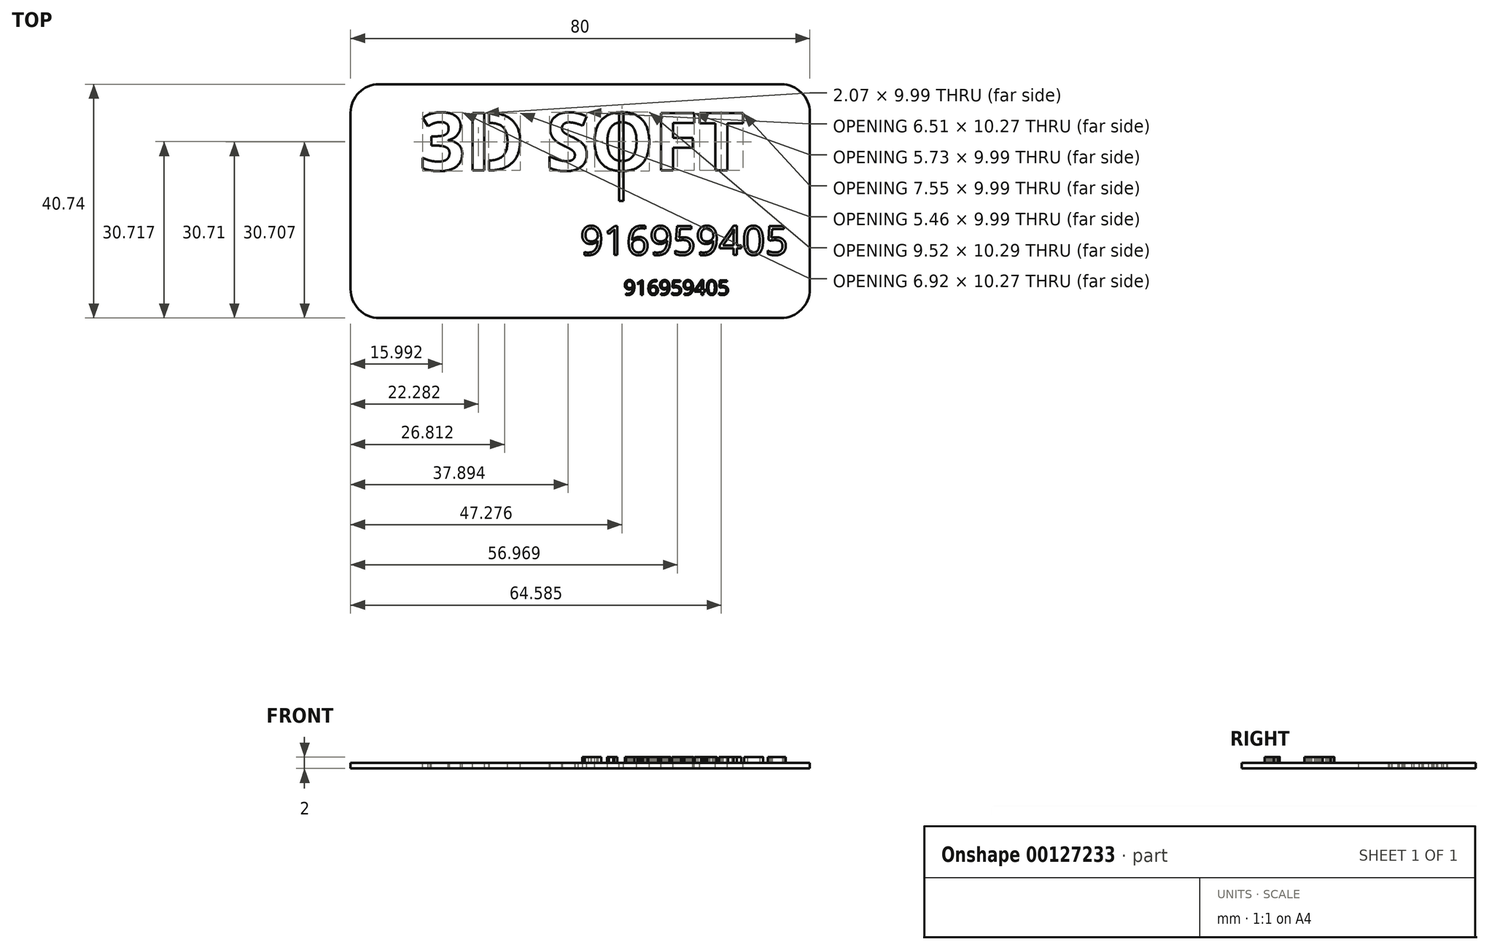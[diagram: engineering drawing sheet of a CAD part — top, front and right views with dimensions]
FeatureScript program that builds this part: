
annotation { "Feature Type Name" : "Feature", "Feature Type Description" : "" }
export const myFeature = defineFeature(function(context is Context, id is Id, definition is map)
    precondition{}
    {
        {
            var Q0;
            Q0=qCreatedBy(makeId("Top.planeOp"),FACE);
            var sketch = newSketch(context, id + "F0", { "sketchPlane" : qUnion([Q0])});
            skLineSegment(sketch, "E0.bottom", {"start": v(40, 20.37) * mm, "end": v(-40, 20.37) * mm});
            skLineSegment(sketch, "E0.top", {"start": v(40, -20.37) * mm, "end": v(-40, -20.37) * mm});
            skLineSegment(sketch, "E0.left", {"start": v(40, 20.37) * mm, "end": v(40, -20.37) * mm});
            skLineSegment(sketch, "E0.right", {"start": v(-40, 20.37) * mm, "end": v(-40, -20.37) * mm});
            skPoint(sketch, "E0.middle", {"position": v(0, 0) * mm});
            skSolve(sketch);
        }
        {
            var Q0;
            Q0=makeQuery(id+"F0.imprint","IMPRINT",FACE,{"disambiguationData":[TD([[makeQuery(id+"F0.imprint","IMPRINT",EDGE,{"derivedFrom":sQuery(id+"F0.wireOp",EDGE,"E0.bottom")}),1.0]])]});
            extrude(context, id + "F1", {"entities" : qUnion([Q0]), "depth" : 1 * mm});
        }
        {
            var Q0;
            Q0=makeQuery(id+"F1.opExtrude","CAP_FACE",FACE,{"disambiguationData":[OSD([sQuery(id+"F0.wireOp",EDGE,"E0.bottom"),sQuery(id+"F0.wireOp",EDGE,"E0.top"),sQuery(id+"F0.wireOp",EDGE,"E0.left"),sQuery(id+"F0.wireOp",EDGE,"E0.right")])],"isStart":false});
            var sketch = newSketch(context, id + "F2", { "sketchPlane" : qUnion([Q0])});
            skText(sketch, "E1", { "text": "3D SOFT", "fontName": "OpenSans-Bold.ttf"});
            const initialGuessF2  = {"E1": [-0.028, 0.00534, 1, 0, 0.01008]};
            skSetInitialGuess(sketch, initialGuessF2);
            skSolve(sketch);
        }
        {
            var Q0;
            Q0 = qSketchRegion(id + "F2", true);
            extrude(context, id + "F3", {"entities" : qUnion([Q0]), "operationType" : NewBodyOperationType.REMOVE, "oppositeDirection" : true, "depth" : 25 * mm});
        }
        {
            var Q0;
            {var subQ0=sQuery(id+"F0.wireOp",EDGE,"E0.top");var subQ1=sQuery(id+"F0.wireOp",EDGE,"E0.right");var subQ2=sQuery(id+"F0.wireOp",EDGE,"E0.bottom");var subQ3=sQuery(id+"F0.wireOp",EDGE,"E0.left");Q0=makeQuery(id+"F3.boolean.opBoolean","SPLIT",FACE,{"disambiguationData":[TD([makeQuery(id+"F1.opExtrude","SWEPT_FACE",FACE,{"disambiguationData":[OSD([subQ2])]})])],"derivedFrom":makeQuery(id+"F1.opExtrude","CAP_FACE",FACE,{"disambiguationData":[OSD([subQ2,subQ0,subQ3,subQ1])],"isStart":false})});}
            var sketch = newSketch(context, id + "F4", { "sketchPlane" : qUnion([Q0])});
            skLineSegment(sketch, "E2", {"start": v(-16.68, 15.34) * mm, "end": v(-16.68, 5.34) * mm});
            skLineSegment(sketch, "E3", {"start": v(-16.68, 5.34) * mm, "end": v(-15.92, 5.34) * mm});
            skLineSegment(sketch, "E4", {"start": v(-15.92, 5.34) * mm, "end": v(-15.92, 15.34) * mm});
            skLineSegment(sketch, "E5", {"start": v(-15.92, 15.34) * mm, "end": v(-16.68, 15.34) * mm});
            skSolve(sketch);
        }
        {
            var Q0;
            {var subQ0=sQuery(id+"F0.wireOp",EDGE,"E0.top");var subQ1=sQuery(id+"F0.wireOp",EDGE,"E0.right");var subQ2=sQuery(id+"F0.wireOp",EDGE,"E0.bottom");var subQ3=sQuery(id+"F0.wireOp",EDGE,"E0.left");Q0=makeQuery(id+"F3.boolean.opBoolean","SPLIT",FACE,{"disambiguationData":[TD([makeQuery(id+"F1.opExtrude","SWEPT_FACE",FACE,{"disambiguationData":[OSD([subQ2])]})])],"derivedFrom":makeQuery(id+"F1.opExtrude","CAP_FACE",FACE,{"disambiguationData":[OSD([subQ2,subQ0,subQ3,subQ1])],"isStart":false})});}
            var sketch = newSketch(context, id + "F5", { "sketchPlane" : qUnion([Q0])});
            skLineSegment(sketch, "E6", {"start": v(6.76, 15.47) * mm, "end": v(6.76, 0) * mm});
            skLineSegment(sketch, "E7", {"start": v(6.76, 0) * mm, "end": v(7.55, 0) * mm});
            skLineSegment(sketch, "E8", {"start": v(7.55, 0) * mm, "end": v(7.55, 15.49) * mm});
            skLineSegment(sketch, "E9", {"start": v(7.55, 15.49) * mm, "end": v(6.76, 15.47) * mm});
            skSolve(sketch);
        }
        {
            var Q0;
            Q0 = qSketchRegion(id + "F5", true);
            extrude(context, id + "F6", {"entities" : qUnion([Q0]), "oppositeDirection" : true, "depth" : 1 * mm});
        }
        {
            var Q0;
            Q0=makeQuery(id+"F1.opExtrude","SWEPT_EDGE",EDGE,{"disambiguationData":[OSD([sQuery(id+"F0.wireOp",EDGE,"E0.bottom"),sQuery(id+"F0.wireOp",EDGE,"E0.left")])]});
            var Q1;
            Q1=makeQuery(id+"F1.opExtrude","SWEPT_EDGE",EDGE,{"disambiguationData":[OSD([sQuery(id+"F0.wireOp",EDGE,"E0.top"),sQuery(id+"F0.wireOp",EDGE,"E0.left")])]});
            var Q2;
            Q2=makeQuery(id+"F1.opExtrude","SWEPT_EDGE",EDGE,{"disambiguationData":[OSD([sQuery(id+"F0.wireOp",EDGE,"E0.top"),sQuery(id+"F0.wireOp",EDGE,"E0.right")])]});
            var Q3;
            Q3=makeQuery(id+"F1.opExtrude","SWEPT_EDGE",EDGE,{"disambiguationData":[OSD([sQuery(id+"F0.wireOp",EDGE,"E0.bottom"),sQuery(id+"F0.wireOp",EDGE,"E0.right")])]});
            fillet(context, id + "F7", {"entities" : qUnion([Q0, Q1, Q2, Q3]), "radius" : 5 * mm, "tangentPropagation" : true, "allowEdgeOverflow" : false});
        }
        {
            var Q0;
            {var subQ0=sQuery(id+"F0.wireOp",EDGE,"E0.top");var subQ1=sQuery(id+"F0.wireOp",EDGE,"E0.right");var subQ2=sQuery(id+"F0.wireOp",EDGE,"E0.bottom");var subQ3=sQuery(id+"F0.wireOp",EDGE,"E0.left");Q0=makeQuery(id+"F3.boolean.opBoolean","SPLIT",FACE,{"disambiguationData":[TD([makeQuery(id+"F1.opExtrude","SWEPT_FACE",FACE,{"disambiguationData":[OSD([subQ2])]})])],"derivedFrom":makeQuery(id+"F1.opExtrude","CAP_FACE",FACE,{"disambiguationData":[OSD([subQ2,subQ0,subQ3,subQ1])],"isStart":false})});}
            var sketch = newSketch(context, id + "F8", { "sketchPlane" : qUnion([Q0])});
            skText(sketch, "E10", { "text": "916959405", "fontName": "OpenSans-Regular.ttf"});
            const initialGuessF8  = {"E10": [0.0076, -0.01635, 1, 0, 0.00257]};
            skSetInitialGuess(sketch, initialGuessF8);
            skSolve(sketch);
        }
        {
            var Q0;
            Q0 = qSketchRegion(id + "F8", true);
            extrude(context, id + "F9", {"entities" : qUnion([Q0]), "operationType" : NewBodyOperationType.ADD, "depth" : 1 * mm});
        }
        {
            var Q0;
            Q0=makeQuery(id+"F4.imprint","IMPRINT",FACE,{"disambiguationData":[TD([[makeQuery(id+"F4.imprint","IMPRINT",EDGE,{"derivedFrom":makeQuery(id+"F1.opExtrude","CAP_EDGE",EDGE,{"disambiguationData":[OSD([sQuery(id+"F0.wireOp",EDGE,"E0.bottom")])],"isStart":false})}),1.0]])]});
            var sketch = newSketch(context, id + "F10", { "sketchPlane" : qUnion([Q0])});
            skText(sketch, "E11", { "text": "916959405", "fontName": "OpenSans-Regular.ttf"});
            const initialGuessF10  = {"E11": [0, -0.00938, 1, 0, 0.00507]};
            skSetInitialGuess(sketch, initialGuessF10);
            skSolve(sketch);
        }
        {
            var Q0;
            Q0 = qSketchRegion(id + "F10", true);
            extrude(context, id + "F11", {"entities" : qUnion([Q0]), "operationType" : NewBodyOperationType.ADD, "depth" : 1 * mm});
        }
        {
            var Q0;
            Q0 = qSketchRegion(id + "F4", true);
            extrude(context, id + "F12", {"entities" : qUnion([Q0]), "operationType" : NewBodyOperationType.ADD, "oppositeDirection" : true, "depth" : 1 * mm});
        }
    });
